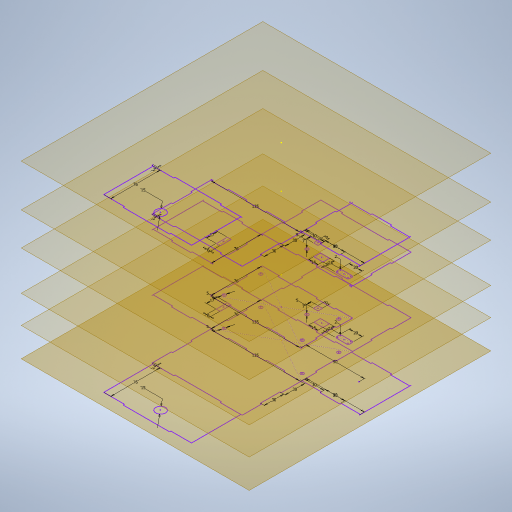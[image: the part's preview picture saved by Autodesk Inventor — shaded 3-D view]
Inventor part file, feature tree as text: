
AUTODESK INVENTOR PART (.ipt)
format: ipt  version: 2023 (Build 270158000, 158)  size: 374,784 bytes
history: native  units: in
note: dims shown in document units (in); Inventor stores cm internally (conversion verified against a paired STEP export)
features: sketch x8, plane x6
ambient origin geometry x8: Origin, YZ Plane, XZ Plane, XY Plane, X Axis, Y Axis, Z Axis, Center Point
feature tree (14):
  sketch  "Sketch1"  dims[d0=5.315in]
  plane  "Work Plane6"
  sketch  "Sketch3"  dims[d1=2.9921in]
  sketch  "Sketch4"  dims[d4=0.0787in]
  sketch  "Sketch5"  dims[d5=0.1969in]
  sketch  "Sketch6"  dims[d7=3.5433in]
  sketch  "Sketch7"  dims[d9=0.0787in]
  sketch  "Sketch8"  dims[d11=1.1811in]
  sketch  "Sketch10"  dims[d12=1.1811in d13=1.1811in d14=1.1811in d16=0.0787in d17=2.9921in d18=0.5906in d19=0.2756in d20=0.2756in d21=0.7874in d22=0.315in d23=0.2362in d24=0.6693in d25=0.1969in d26=0.0787in d27=0.5512in d28=0.3937in d29=0.0in d30=1.75in d31=1.6875in d32=2.375in d33=2.0in d34=2.5625in d35=5.315in d36=2.9921in d37=0.1969in d38=3.5433in d39=2.9921in d40=0.2362in d41=0.6693in d42=3.5433in d43=1.1811in d44=1.1811in d45=5.315in d46=3.5433in d47=1.1811in d48=1.1811in d49=0.0787in d50=0.2756in d51=0.2756in d52=0.7874in d53=0.315in d54=0.1969in d55=0.0787in d56=0.5512in d57=0.3937in d58=0.0787in d59=2.9921in d60=0.5906in]
  plane  "Work Plane1"
  plane  "Work Plane2"
  plane  "Work Plane3"
  plane  "Work Plane4"
  plane  "Work Plane5"
